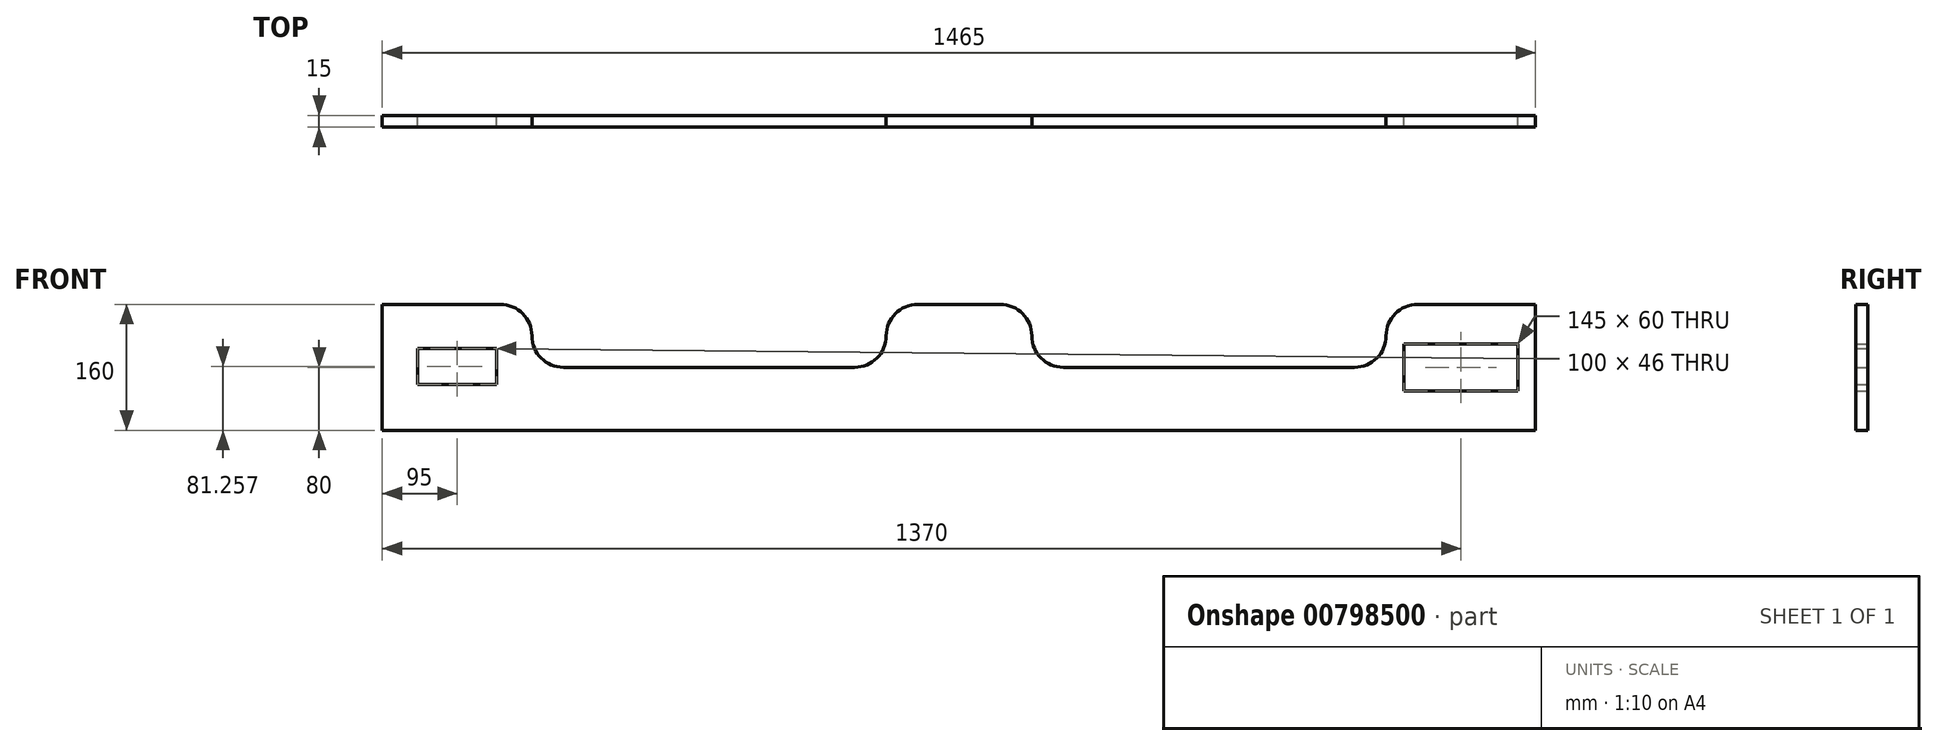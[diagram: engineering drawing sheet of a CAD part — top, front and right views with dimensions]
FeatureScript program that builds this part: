
annotation { "Feature Type Name" : "Feature", "Feature Type Description" : "" }
export const myFeature = defineFeature(function(context is Context, id is Id, definition is map)
    precondition{}
    {
        {
            var Q0;
            Q0=qCreatedBy(makeId("Front.planeOp"),FACE);
            var sketch = newSketch(context, id + "F0", { "sketchPlane" : qUnion([Q0])});
            skLineSegment(sketch, "E0", {"start": v(0, 0) * mm, "end": v(0, -160) * mm});
            skLineSegment(sketch, "E1", {"start": v(0, -160) * mm, "end": v(1465, -160) * mm});
            skLineSegment(sketch, "E2", {"start": v(1465, -160) * mm, "end": v(1465, 0) * mm});
            skLineSegment(sketch, "E3", {"start": v(1315, 0) * mm, "end": v(1465, 0) * mm});
            skLineSegment(sketch, "E4", {"start": v(1275, -40) * mm, "end": v(1275, -40) * mm});
            skLineSegment(sketch, "E5", {"start": v(1235, -80) * mm, "end": v(865, -80) * mm});
            skLineSegment(sketch, "E6", {"start": v(825, -40) * mm, "end": v(825, -40) * mm});
            skLineSegment(sketch, "E7", {"start": v(785, 0) * mm, "end": v(680, 0) * mm});
            skLineSegment(sketch, "E8", {"start": v(640, -40) * mm, "end": v(640, -40) * mm});
            skLineSegment(sketch, "E9", {"start": v(600, -80) * mm, "end": v(230, -80) * mm});
            skLineSegment(sketch, "E10", {"start": v(190, -40) * mm, "end": v(190, -40) * mm});
            skLineSegment(sketch, "E11", {"start": v(150, 0) * mm, "end": v(0, 0) * mm});
            skPoint(sketch, "E12.visualSharp", {"position": v(640, 0) * mm});
            skArc(sketch, "E12.filletArc", {"start": v(680, 0) * mm, "mid": v(651.72, -11.72) * mm, "end": v(640, -40) * mm});
            skPoint(sketch, "E13.visualSharp", {"position": v(825, 0) * mm});
            skArc(sketch, "E13.filletArc", {"start": v(825, -40) * mm, "mid": v(813.28, -11.72) * mm, "end": v(785, 0) * mm});
            skPoint(sketch, "E14.visualSharp", {"position": v(825, -80) * mm});
            skArc(sketch, "E14.filletArc", {"start": v(825, -40) * mm, "mid": v(836.72, -68.28) * mm, "end": v(865, -80) * mm});
            skPoint(sketch, "E15.visualSharp", {"position": v(1275, -80) * mm});
            skArc(sketch, "E15.filletArc", {"start": v(1235, -80) * mm, "mid": v(1263.28, -68.28) * mm, "end": v(1275, -40) * mm});
            skPoint(sketch, "E16.visualSharp", {"position": v(1275, 0) * mm});
            skArc(sketch, "E16.filletArc", {"start": v(1315, 0) * mm, "mid": v(1286.72, -11.72) * mm, "end": v(1275, -40) * mm});
            skPoint(sketch, "E17.visualSharp", {"position": v(640, -80) * mm});
            skArc(sketch, "E17.filletArc", {"start": v(600, -80) * mm, "mid": v(628.28, -68.28) * mm, "end": v(640, -40) * mm});
            skPoint(sketch, "E18.visualSharp", {"position": v(190, -80) * mm});
            skArc(sketch, "E18.filletArc", {"start": v(190, -40) * mm, "mid": v(201.72, -68.28) * mm, "end": v(230, -80) * mm});
            skPoint(sketch, "E19.visualSharp", {"position": v(190, 0) * mm});
            skArc(sketch, "E19.filletArc", {"start": v(190, -40) * mm, "mid": v(178.28, -11.72) * mm, "end": v(150, 0) * mm});
            skLineSegment(sketch, "E20", {"start": v(1370, 15.77) * mm, "end": v(1370, -184.05) * mm, "construction": true});
            skLineSegment(sketch, "E21", {"start": v(1465, -80) * mm, "end": v(1243.18, -80) * mm, "construction": true});
            skLineSegment(sketch, "E22.bottom", {"start": v(1442.5, -110) * mm, "end": v(1297.5, -110) * mm});
            skLineSegment(sketch, "E22.top", {"start": v(1442.5, -50) * mm, "end": v(1297.5, -50) * mm});
            skLineSegment(sketch, "E22.left", {"start": v(1442.5, -110) * mm, "end": v(1442.5, -50) * mm});
            skLineSegment(sketch, "E22.right", {"start": v(1297.5, -110) * mm, "end": v(1297.5, -50) * mm});
            skPoint(sketch, "E22.middle", {"position": v(1370, -80) * mm});
            skLineSegment(sketch, "E23", {"start": v(95, 19.87) * mm, "end": v(95, -177.36) * mm, "construction": true});
            skLineSegment(sketch, "E24", {"start": v(0, -80) * mm, "end": v(230, -80) * mm, "construction": true});
            skLineSegment(sketch, "E25.bottom", {"start": v(145, -101.74) * mm, "end": v(45, -101.74) * mm});
            skLineSegment(sketch, "E25.top", {"start": v(145, -55.74) * mm, "end": v(45, -55.74) * mm});
            skLineSegment(sketch, "E25.left", {"start": v(145, -101.74) * mm, "end": v(145, -55.74) * mm});
            skLineSegment(sketch, "E25.right", {"start": v(45, -101.74) * mm, "end": v(45, -55.74) * mm});
            skPoint(sketch, "E25.middle", {"position": v(95, -78.74) * mm});
            skSolve(sketch);
        }
        {
            var Q0;
            Q0=makeQuery(id+"F0.imprint","IMPRINT",FACE,{"disambiguationData":[TD([[makeQuery(id+"F0.imprint","IMPRINT",EDGE,{"derivedFrom":sQuery(id+"F0.wireOp",EDGE,"E0")}),1.0]])]});
            extrude(context, id + "F1", {"entities" : qUnion([Q0]), "depth" : 15 * mm, "offsetDistance" : 25 * mm});
        }
    });
